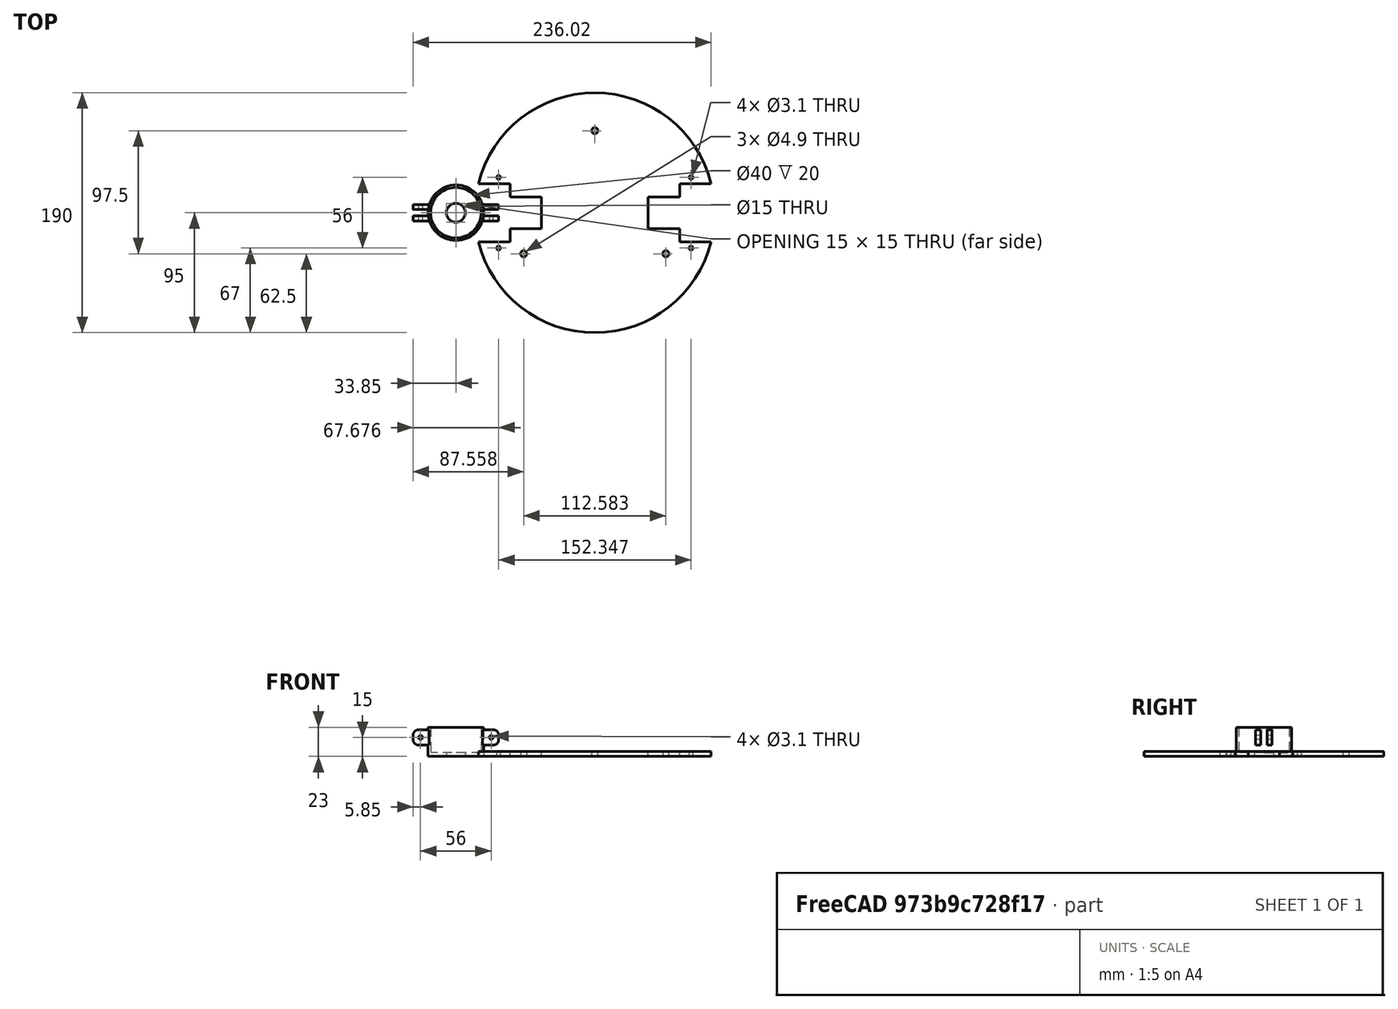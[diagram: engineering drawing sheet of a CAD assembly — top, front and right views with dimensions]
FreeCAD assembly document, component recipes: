
FREECAD ASSEMBLY — COMPONENT RECIPES ("GyroBot")

This assembly document has 2 components, labeled P0..P1 below (a component is one placed body or linked part). 2 of them carry a construction recipe — the FreeCAD feature program that regenerates the part from scratch, quoted from this document or its linked companion documents; the rest are supplied as boundary geometry only. No exploded tour is included for this assembly.
COMPONENT P0 — recipe-attached ("MotorMount", modeled in this document).
Construction recipe (the document's own serialized feature program — sketch geometry with constraints, then the solid features built on it; lengths are millimeters unless a unit is written):

FEATURE [Sketcher::SketchObject] Sketch
  ArcFitTolerance = 1e-06
  AttachmentSupport = -> [XY_Plane]
  FullyConstrained = false
  MakeInternals = false
  MapMode = 5
  sketch-geometry (2):
    g0: Circle CenterX=0 CenterY=0 CenterZ=0 NormalX=0 NormalY=0 NormalZ=1 AngleXU=0 Radius=22
    g1: Circle CenterX=0 CenterY=0 CenterZ=0 NormalX=0 NormalY=0 NormalZ=1 AngleXU=0 Radius=7.5
  constraints (2):
    c: Diameter(g0) = 44
    c: Diameter(g1) = 15
FEATURE [PartDesign::Pad] Pad
  Direction = (0,0,1)
  Length = 3
  Length2 = 10
  Profile = -> Sketch
  ReferenceAxis = -> Sketch [N_Axis]
  Refine = true
  Suppressed = false
  Type = 0
FEATURE [Sketcher::SketchObject] Sketch001
  ArcFitTolerance = 1e-06
  AttachmentSupport = -> [Pad]
  FullyConstrained = true
  MakeInternals = false
  MapMode = 5
  Placement = pos=(0,0,3) rot=(0,0,1;0rad)
  sketch-geometry (2):
    g0: Circle CenterX=0 CenterY=0 CenterZ=0 NormalX=0 NormalY=0 NormalZ=1 AngleXU=0 Radius=22
    g1: Circle CenterX=0 CenterY=0 CenterZ=0 NormalX=0 NormalY=0 NormalZ=1 AngleXU=0 Radius=20
  constraints (4):
    c: Diameter(g0) = 44
    c: Coincident(g0,g-1)
    c: Diameter(g1) = 40
    c: Coincident(g1,g0)
FEATURE [PartDesign::Pad] Pad001
  BaseFeature = -> Pad
  Direction = (0,0,1)
  Length = 20
  Length2 = 10
  Profile = -> Sketch001
  ReferenceAxis = -> Sketch001 [N_Axis]
  Refine = true
  Suppressed = false
  Type = 0
  UseCustomVector = true
FEATURE [PartDesign::Plane] DatumPlane
  AttachmentOffset = pos=(0,0,2.5) rot=(0,0,1;0rad)
  AttachmentSupport = -> [Pad001]
  Length = 79.3297
  MapMode = 3
  Placement = pos=(0,-2.5,6e-16) rot=(1,0,0;1.5708rad)
  ResizeMode = 0
  Width = 61.6356
FEATURE [Sketcher::SketchObject] Sketch002
  ArcFitTolerance = 1e-06
  AttachmentSupport = -> [DatumPlane]
  ExternalGeometry = -> [Pad001]
  FullyConstrained = false
  MakeInternals = false
  MapMode = 5
  Placement = pos=(0,-2.5,6e-16) rot=(1,0,0;1.5708rad)
  sketch-geometry (4):
    g0: LineSegment StartX=20.847 StartY=20.9308 StartZ=0 EndX=20.847 EndY=8.93082 EndZ=0
    g1: LineSegment StartX=20.847 StartY=8.93082 StartZ=0 EndX=33.847 EndY=8.93082 EndZ=0
    g2: LineSegment StartX=33.847 StartY=8.93082 StartZ=0 EndX=33.847 EndY=20.9308 EndZ=0
    g3: LineSegment StartX=33.847 StartY=20.9308 StartZ=0 EndX=20.847 EndY=20.9308 EndZ=0
  constraints (10):
    c: Coincident(g0,g1)
    c: Coincident(g1,g2)
    c: Coincident(g2,g3)
    c: Coincident(g3,g0)
    c: Vertical(g0)
    c: Vertical(g2)
    c: Horizontal(g1)
    c: Horizontal(g3)
    c: Distance(g0,g2) = 13
    c: Distance(g1,g3) = 12
FEATURE [PartDesign::Pad] Pad002
  BaseFeature = -> Pad001
  Direction = (0,-1,2e-16)
  Length = 4
  Length2 = 10
  Profile = -> Sketch002
  ReferenceAxis = -> Sketch002 [N_Axis]
  Refine = true
  Suppressed = false
  Type = 0
FEATURE [PartDesign::Mirrored] Mirrored
  BaseFeature = -> Pad002
  MirrorPlane = -> XZ_Plane
  Originals = -> [Pad002]
  Refine = true
  Suppressed = false
  TransformMode = 0
FEATURE [Sketcher::SketchObject] Sketch003
  ArcFitTolerance = 1e-06
  AttachmentSupport = -> [XZ_Plane]
  FullyConstrained = true
  MakeInternals = false
  MapMode = 5
  Placement = pos=(0,0,0) rot=(1,0,0;1.5708rad)
  sketch-geometry (1):
    g0: Circle CenterX=28 CenterY=15 CenterZ=0 NormalX=0 NormalY=0 NormalZ=1 AngleXU=0 Radius=1.55
  constraints (3):
    c: Diameter(g0) = 3.1
    c: DistanceX(g-1,g0) = 28
    c: Distance(g0,g-1) = 15
FEATURE [PartDesign::Pocket] Pocket
  BaseFeature = -> Mirrored
  Direction = (0,1,-2e-16)
  Length = 30
  Length2 = 5
  Midplane = true
  Profile = -> Sketch003
  ReferenceAxis = -> Sketch003 [N_Axis]
  Refine = true
  Suppressed = false
  Type = 0
FEATURE [PartDesign::Fillet] Fillet
  Base = -> Pocket [Edge27]
  BaseFeature = -> Pocket
  Radius = 4
  Refine = true
  SupportTransform = false
  Suppressed = false
  UseAllEdges = false
FEATURE [PartDesign::Fillet] Fillet001
  Base = -> Fillet [Edge24,Edge29,Edge35]
  BaseFeature = -> Fillet
  Radius = 4
  Refine = true
  SupportTransform = false
  Suppressed = false
  UseAllEdges = false
FEATURE [PartDesign::Mirrored] Mirrored001
  BaseFeature = -> Fillet001
  MirrorPlane = -> YZ_Plane
  Originals = -> [Fillet001]
  Refine = true
  Suppressed = false
  TransformMode = 1
FEATURE [PartDesign::CoordinateSystem] motor_screw
  AttacherType = Attacher::AttachEngine3D
  AttachmentSupport = -> [Mirrored001]
  MapMode = 11
  Placement = pos=(28,-2.5,15) rot=(0.57735,-0.57735,0.57735;2.0944rad)
FEATURE [PartDesign::Body] Body  label="MotorMount"
  AllowCompound = false
  Group = -> [Sketch,Pad,Sketch001,Pad001,DatumPlane,Sketch002,Pad002,Mirrored,Sketch003,Pocket,Fillet,Fillet001,Mirrored001,motor_screw]
  Origin = -> Origin
  Placement = pos=(-110,0,0) rot=(0,0,1;0rad)
  Tip = -> Mirrored001
COMPONENT P1 — recipe-attached ("GyroBase", modeled in this document).
Construction recipe (the document's own serialized feature program — sketch geometry with constraints, then the solid features built on it; lengths are millimeters unless a unit is written):

FEATURE [Sketcher::SketchObject] Sketch004
  ArcFitTolerance = 1e-06
  AttachmentSupport = -> [XY_Plane001]
  FullyConstrained = false
  MakeInternals = false
  MapMode = 5
  sketch-geometry (27):
    g0: ArcOfCircle CenterX=0 CenterY=0 CenterZ=0 NormalX=0 NormalY=0 NormalZ=1 AngleXU=0 Radius=95 StartAngle=0.244535 EndAngle=2.89706
    g1: Circle CenterX=0 CenterY=65 CenterZ=0 NormalX=0 NormalY=0 NormalZ=1 AngleXU=0 Radius=2.45
    g2: Circle CenterX=56.2917 CenterY=-32.5 CenterZ=0 NormalX=0 NormalY=0 NormalZ=1 AngleXU=0 Radius=2.45
    g3: LineSegment StartX=67.1737 StartY=-23 StartZ=0 EndX=92.1737 EndY=-23 EndZ=0
    g4: LineSegment StartX=92.1737 StartY=23 StartZ=0 EndX=67.1737 EndY=23 EndZ=0
    g5: LineSegment StartX=67.1737 StartY=23 StartZ=0 EndX=67.1737 EndY=12.5 EndZ=0
    g6: GeomPoint [constr] X=79.6737 Y=0 Z=0
    g7: LineSegment StartX=42.1737 StartY=-12.5 StartZ=0 EndX=67.1737 EndY=-12.5 EndZ=0
    g8: LineSegment StartX=67.1737 StartY=12.5 StartZ=0 EndX=42.1737 EndY=12.5 EndZ=0
    g9: LineSegment StartX=42.1737 StartY=12.5 StartZ=0 EndX=42.1737 EndY=-12.5 EndZ=0
    g10: GeomPoint [constr] X=54.6737 Y=0 Z=0
    g11: LineSegment StartX=67.1737 StartY=-12.5 StartZ=0 EndX=67.1737 EndY=-23 EndZ=0
    g12: Circle CenterX=76.1737 CenterY=28 CenterZ=0 NormalX=0 NormalY=0 NormalZ=1 AngleXU=0 Radius=1.55
    g13: Circle CenterX=76.1737 CenterY=-28 CenterZ=0 NormalX=0 NormalY=0 NormalZ=1 AngleXU=0 Radius=1.55
    g14: Circle CenterX=-56.2917 CenterY=-32.5 CenterZ=0 NormalX=0 NormalY=0 NormalZ=1 AngleXU=0 Radius=2.45
    g15: LineSegment StartX=-67.1737 StartY=-23 StartZ=0 EndX=-92.1737 EndY=-23 EndZ=0
    g16: LineSegment StartX=-92.1737 StartY=23 StartZ=0 EndX=-67.1737 EndY=23 EndZ=0
    g17: LineSegment StartX=-67.1737 StartY=23 StartZ=0 EndX=-67.1737 EndY=12.5 EndZ=0
    g18: GeomPoint [constr] X=-79.6737 Y=0 Z=0
    g19: LineSegment StartX=-42.1737 StartY=-12.5 StartZ=0 EndX=-67.1737 EndY=-12.5 EndZ=0
    g20: LineSegment StartX=-67.1737 StartY=12.5 StartZ=0 EndX=-42.1737 EndY=12.5 EndZ=0
    g21: LineSegment StartX=-42.1737 StartY=12.5 StartZ=0 EndX=-42.1737 EndY=-12.5 EndZ=0
    g22: GeomPoint [constr] X=-54.6737 Y=0 Z=0
    g23: LineSegment StartX=-67.1737 StartY=-12.5 StartZ=0 EndX=-67.1737 EndY=-23 EndZ=0
    g24: Circle CenterX=-76.1737 CenterY=28 CenterZ=0 NormalX=0 NormalY=0 NormalZ=1 AngleXU=0 Radius=1.55
    g25: Circle CenterX=-76.1737 CenterY=-28 CenterZ=0 NormalX=0 NormalY=0 NormalZ=1 AngleXU=0 Radius=1.55
    g26: ArcOfCircle CenterX=0 CenterY=0 CenterZ=0 NormalX=0 NormalY=0 NormalZ=1 AngleXU=0 Radius=95 StartAngle=3.38613 EndAngle=6.03865
  constraints (56):
    c: Diameter(g0) = 190
    c: Coincident(g0,g-1)
    c: Diameter(g1) = 4.9
    c: PointOnObject(g1,g-2)
    c: DistanceY(g-1,g1) = 65
    c: Diameter(g2) = 4.9
    c: Coincident(g4,g5)
    c: Coincident(g11,g3)
    c: Horizontal(g3)
    c: Horizontal(g4)
    c: Vertical(g5)
    c: Symmetric(g4,g3,g6)
    c: Distance(g3,g11) = 25
    c: Distance(g3,g4) = 46
    c: PointOnObject(g6,g-1)
    c: Coincident(g8,g9)
    c: Coincident(g9,g7)
    c: Horizontal(g7)
    c: Horizontal(g8)
    c: Vertical(g9)
    c: Symmetric(g8,g7,g10)
    c: Distance(g7,g9) = 25
    c: Distance(g7,g8) = 25
    c: PointOnObject(g10,g-1)
    c: PointOnObject(g11,g7)
    c: Diameter(g12) = 3.1
    c: DistanceY(g-1,g12) = 28
    c: Block(g5)
    c: Distance(g12,g5) = 9
    c: Diameter(g13) = 3.1
    c: Diameter(g14) = 4.9
    c: Coincident(g16,g17)
    c: Coincident(g23,g15)
    c: Horizontal(g15)
    c: Horizontal(g16)
    c: Vertical(g17)
    c: Symmetric(g16,g15,g18)
    c: Distance(g15,g23) = 25
    c: Distance(g15,g16) = 46
    c: Coincident(g20,g21)
    c: Coincident(g21,g19)
    c: Horizontal(g19)
    c: Horizontal(g20)
    c: Vertical(g21)
    c: Symmetric(g20,g19,g22)
    c: Distance(g19,g21) = 25
    c: Distance(g19,g20) = 25
    c: PointOnObject(g23,g19)
    c: Diameter(g24) = 3.1
    c: Block(g17)
    c: Distance(g24,g17) = 9
    c: Diameter(g25) = 3.1
    c: Coincident(g26,g3)
    c: Equal(g0,g26)
    c: PointOnObject(g26,g15)
    c: Coincident(g0,g26)
FEATURE [PartDesign::Pad] Pad003
  Direction = (0,0,1)
  Length = 4
  Length2 = 10
  Profile = -> Sketch004
  ReferenceAxis = -> Sketch004 [N_Axis]
  Refine = true
  Suppressed = false
  Type = 0
FEATURE [Sketcher::SketchObject] Sketch005
  ArcFitTolerance = 1e-06
  AttachmentSupport = -> [XY_Plane001]
  FullyConstrained = true
  MakeInternals = false
  MapMode = 5
FEATURE [PartDesign::CoordinateSystem] Base_Center
  AttacherType = Attacher::AttachEngine3D
  AttachmentSupport = -> [Pad003]
  MapMode = 5
  Placement = pos=(0,0,0) rot=(1,0,0;3.14159rad)
FEATURE [PartDesign::CoordinateSystem] screw_hole1
  AttacherType = Attacher::AttachEngine3D
  AttachmentSupport = -> [Pad003]
  MapMode = 11
  Placement = pos=(-76.1737,-28,4) rot=(0,0,1;1.5708rad)
FEATURE [PartDesign::CoordinateSystem] screw_hole2
  AttacherType = Attacher::AttachEngine3D
  AttachmentSupport = -> [Pad003]
  MapMode = 11
  Placement = pos=(76.1737,28,4) rot=(0,0,1;1.5708rad)
FEATURE [PartDesign::Body] Body001  label="GyroBase"
  AllowCompound = false
  Group = -> [Sketch004,Pad003,Sketch005,Base_Center,screw_hole1,screw_hole2]
  Origin = -> Origin001
  Tip = -> Pad003
PROVENANCE & LICENSES
A FreeCAD (.FCStd) document from a public repository crawl; recipes are the document's own serialized feature recipes (and, for linked parts, companion documents' recipes).
License: as declared in the source repository (recorded in the dataset sidecar).
